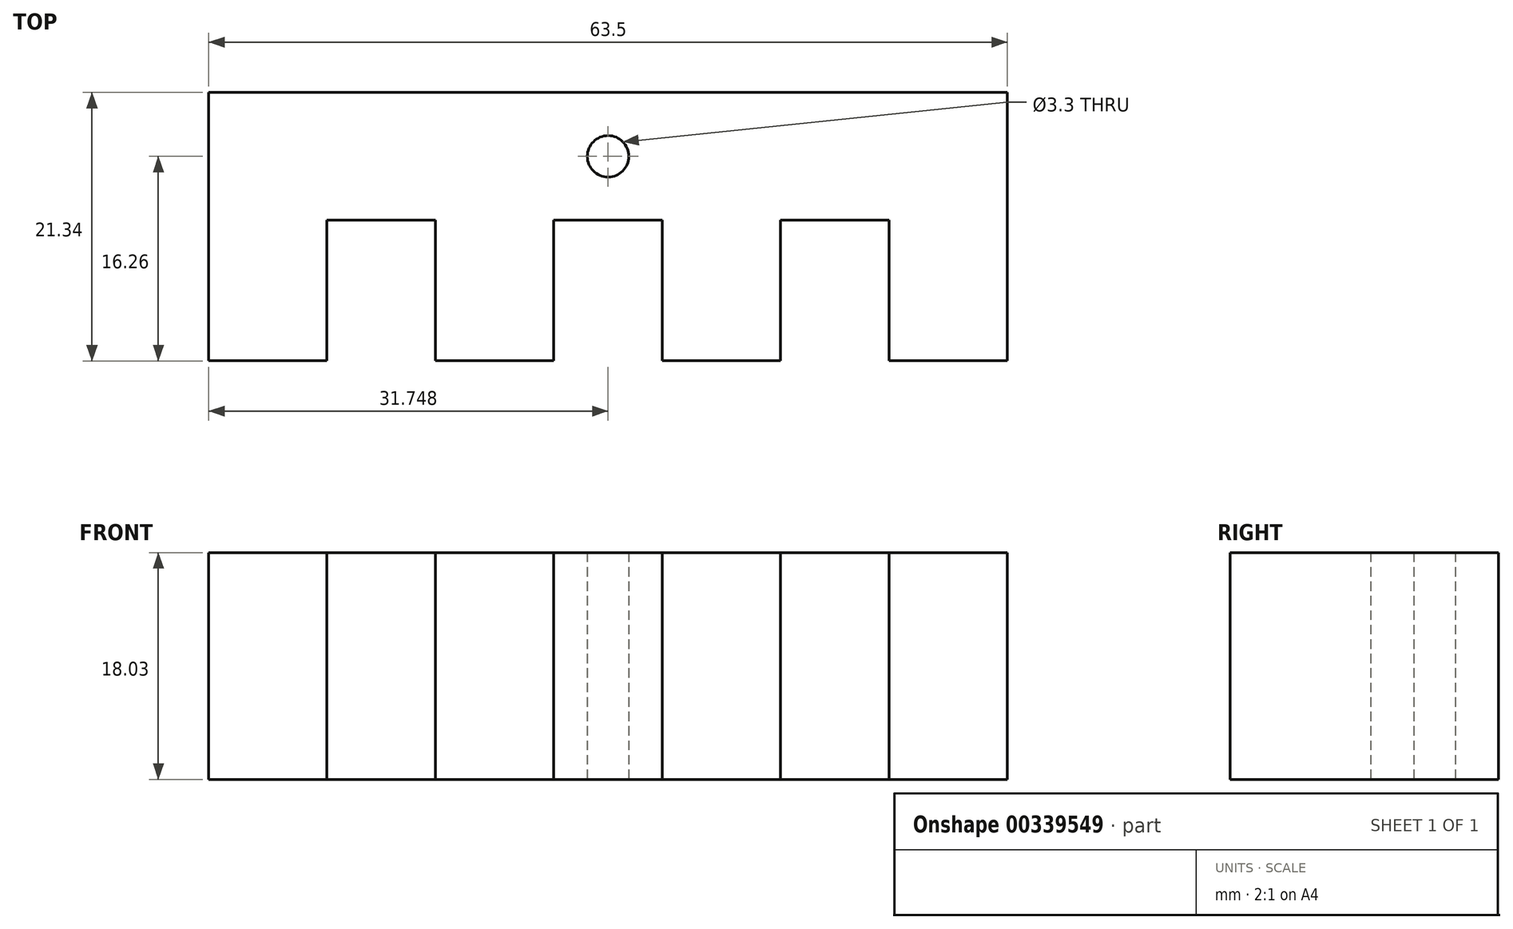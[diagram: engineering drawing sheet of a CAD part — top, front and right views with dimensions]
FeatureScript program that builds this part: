
annotation { "Feature Type Name" : "Feature", "Feature Type Description" : "" }
export const myFeature = defineFeature(function(context is Context, id is Id, definition is map)
    precondition{}
    {
        {
            var Q0;
            Q0=qCreatedBy(makeId("Top.planeOp"),FACE);
            var sketch = newSketch(context, id + "F0", { "sketchPlane" : qUnion([Q0])});
            skLineSegment(sketch, "E0", {"start": v(-54.1, 0) * mm, "end": v(-54.1, -11.18) * mm});
            skLineSegment(sketch, "E1", {"start": v(-54.1, -11.18) * mm, "end": v(-44.7, -11.18) * mm});
            skLineSegment(sketch, "E2", {"start": v(-44.7, -11.18) * mm, "end": v(-44.7, 0) * mm});
            skLineSegment(sketch, "E3", {"start": v(-44.7, 0) * mm, "end": v(-36.07, 0) * mm});
            skLineSegment(sketch, "E4", {"start": v(-36.07, 0) * mm, "end": v(-36.07, -11.18) * mm});
            skLineSegment(sketch, "E5", {"start": v(-36.07, -11.18) * mm, "end": v(-26.67, -11.18) * mm});
            skLineSegment(sketch, "E6", {"start": v(-26.67, -11.18) * mm, "end": v(-26.67, 0) * mm});
            skLineSegment(sketch, "E7", {"start": v(-26.67, 0) * mm, "end": v(-18.03, 0) * mm});
            skLineSegment(sketch, "E8", {"start": v(-18.03, 0) * mm, "end": v(-18.03, -11.18) * mm});
            skLineSegment(sketch, "E9", {"start": v(-18.03, -11.18) * mm, "end": v(-8.64, -11.18) * mm});
            skLineSegment(sketch, "E10", {"start": v(-8.64, -11.18) * mm, "end": v(-8.64, 0) * mm});
            skLineSegment(sketch, "E11", {"start": v(-8.64, 0) * mm, "end": v(0, 0) * mm});
            skLineSegment(sketch, "E12", {"start": v(0, 0) * mm, "end": v(0, -11.18) * mm});
            skLineSegment(sketch, "E13", {"start": v(0, -11.18) * mm, "end": v(9.4, -11.18) * mm});
            skLineSegment(sketch, "E14", {"start": v(9.4, -11.18) * mm, "end": v(9.4, 10.16) * mm});
            skLineSegment(sketch, "E15", {"start": v(9.4, 10.16) * mm, "end": v(-54.1, 10.16) * mm});
            skLineSegment(sketch, "E16", {"start": v(-54.1, 10.16) * mm, "end": v(-54.1, 0) * mm});
            skCircle(sketch, "E17", {"center": v(-22.35, 5.08) * mm, "radius": 1.65 * mm});
            skSolve(sketch);
        }
        {
            var Q0;
            Q0 = qSketchRegion(id + "F0", true);
            extrude(context, id + "F1", {"entities" : qUnion([Q0]), "depth" : 18.03 * mm});
        }
    });
